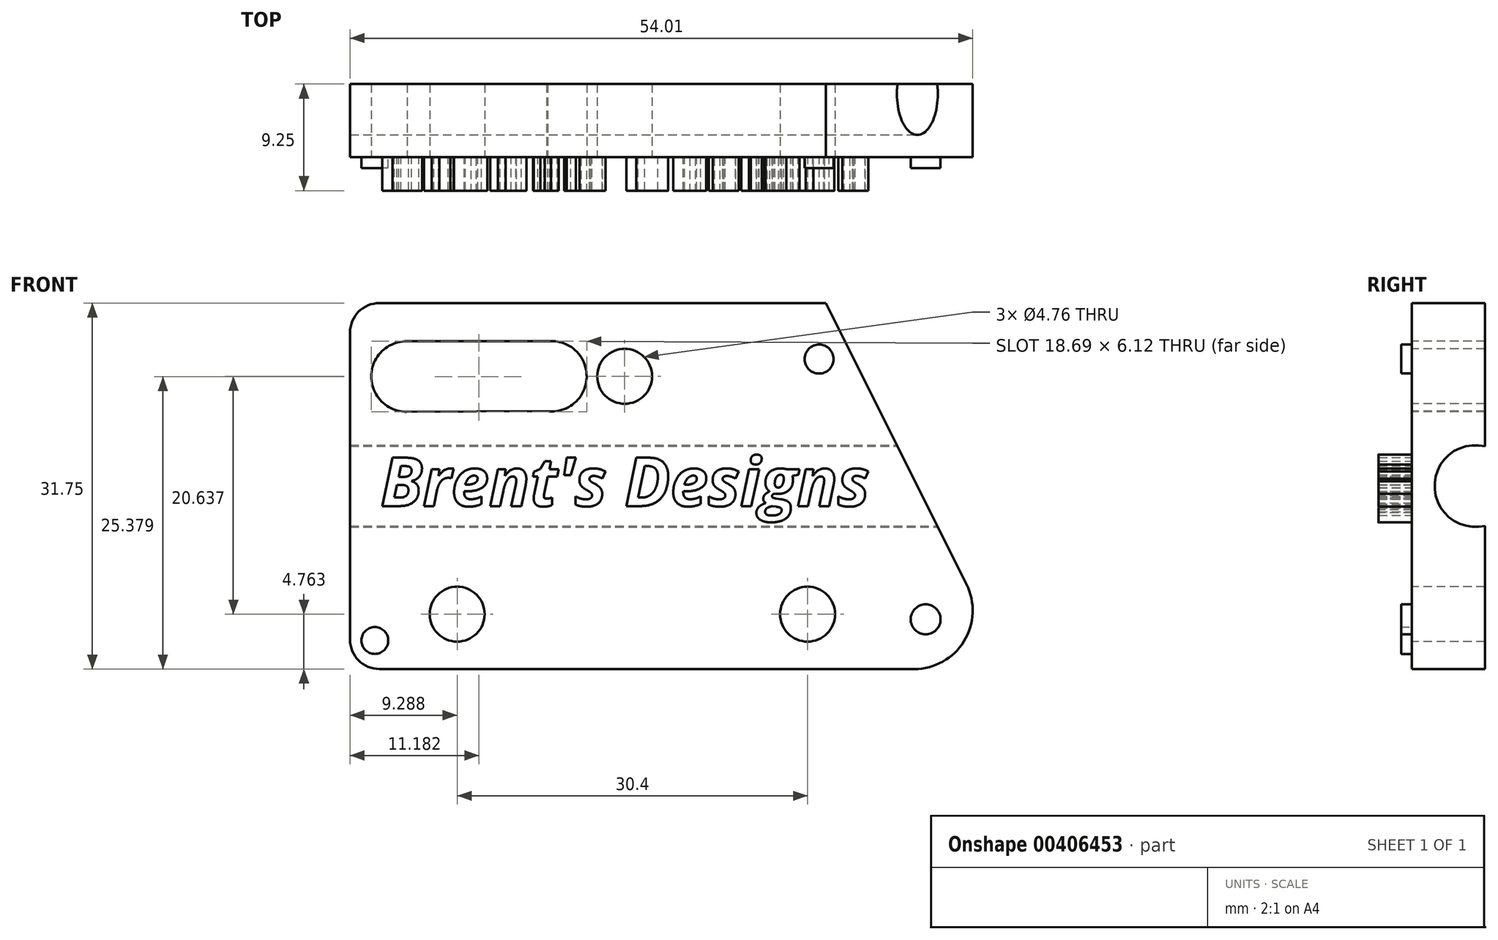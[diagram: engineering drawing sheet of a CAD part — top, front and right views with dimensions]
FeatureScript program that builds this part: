
annotation { "Feature Type Name" : "Feature", "Feature Type Description" : "" }
export const myFeature = defineFeature(function(context is Context, id is Id, definition is map)
    precondition{}
    {
        {
            var Q0;
            Q0=qCreatedBy(makeId("Right.planeOp"),FACE);
            var sketch = newSketch(context, id + "F0", { "sketchPlane" : qUnion([Q0])});
            skLineSegment(sketch, "E0.bottom", {"start": v(0, 0) * mm, "end": v(6.35, 0) * mm});
            skLineSegment(sketch, "E0.top", {"start": v(0, 31.75) * mm, "end": v(6.35, 31.75) * mm});
            skLineSegment(sketch, "E0.left", {"start": v(0, 0) * mm, "end": v(0, 31.75) * mm});
            skLineSegment(sketch, "E1", {"start": v(6.35, 31.75) * mm, "end": v(6.35, 19.33) * mm});
            skArc(sketch, "E2", {"start": v(6.35, 19.33) * mm, "mid": v(1.94, 15.88) * mm, "end": v(6.35, 12.42) * mm});
            skPoint(sketch, "E3.start.orphan", {"position": v(6.35, 15.88) * mm});
            skLineSegment(sketch, "E4.trimOffspring", {"start": v(6.35, 12.42) * mm, "end": v(6.35, 0) * mm});
            skSolve(sketch);
        }
        {
            var Q0;
            Q0=makeQuery(id+"F0.imprint","IMPRINT",FACE,{"disambiguationData":[TD([[makeQuery(id+"F0.imprint","IMPRINT",EDGE,{"derivedFrom":sQuery(id+"F0.wireOp",EDGE,"E0.bottom")}),1.0]])]});
            extrude(context, id + "F1", {"entities" : qUnion([Q0]), "oppositeDirection" : true, "depth" : 57.15 * mm});
        }
        {
            var Q0;
            Q0=makeQuery(id+"F1.opExtrude","SWEPT_FACE",FACE,{"disambiguationData":[OSD([sQuery(id+"F0.wireOp",EDGE,"E0.left")])]});
            var sketch = newSketch(context, id + "F2", { "sketchPlane" : qUnion([Q0])});
            skLineSegment(sketch, "E5", {"start": v(0, 31.75) * mm, "end": v(-15.88, 31.75) * mm});
            skLineSegment(sketch, "E6", {"start": v(-15.88, 31.75) * mm, "end": v(0, 0) * mm});
            skLineSegment(sketch, "E7", {"start": v(0, 0) * mm, "end": v(0, 31.75) * mm});
            skSolve(sketch);
        }
        {
            var Q0;
            Q0=makeQuery(id+"F2.imprint","IMPRINT",FACE,{"disambiguationData":[TD([[makeQuery(id+"F2.imprint","IMPRINT",EDGE,{"derivedFrom":sQuery(id+"F2.wireOp",EDGE,"E5")}),-1.0]])]});
            extrude(context, id + "F3", {"entities" : qUnion([Q0]), "operationType" : NewBodyOperationType.REMOVE, "oppositeDirection" : true, "depth" : 10.92 * mm});
        }
        {
            var Q0;
            Q0=makeQuery(id+"F1.opExtrude","SWEPT_FACE",FACE,{"disambiguationData":[OSD([sQuery(id+"F0.wireOp",EDGE,"E0.left")])]});
            var sketch = newSketch(context, id + "F4", { "sketchPlane" : qUnion([Q0])});
            skSolve(sketch);
        }
        {
            var Q0;
            {var subQ0=sQuery(id+"F0.wireOp",EDGE,"E0.bottom");Q0=makeQuery(id+"F3.boolean.opBoolean","MERGE",EDGE,{"derivedFrom":[makeQuery(id+"F1.opExtrude","CAP_EDGE",EDGE,{"disambiguationData":[OSD([subQ0])],"isStart":true}),makeQuery(id+"F3.opExtrude","SWEPT_EDGE",EDGE,{"disambiguationData":[OSD([subQ0,sQuery(id+"F0.wireOp",EDGE,"E0.left"),sQuery(id+"F2.wireOp",EDGE,"E6"),sQuery(id+"F2.wireOp",EDGE,"E7")])]})]});}
            fillet(context, id + "F5", {"entities" : qUnion([Q0]), "radius" : 5.08 * mm, "tangentPropagation" : true, "allowEdgeOverflow" : false});
        }
        {
            var Q0;
            Q0=makeQuery(id+"F1.opExtrude","CAP_EDGE",EDGE,{"disambiguationData":[OSD([sQuery(id+"F0.wireOp",EDGE,"E0.top")])],"isStart":false});
            var Q1;
            Q1=makeQuery(id+"F1.opExtrude","CAP_EDGE",EDGE,{"disambiguationData":[OSD([sQuery(id+"F0.wireOp",EDGE,"E0.bottom")])],"isStart":false});
            var Q2;
            Q2=makeQuery(id+"F3.boolean.opBoolean","COPY",EDGE,{"derivedFrom":makeQuery(id+"F3.opExtrude","SWEPT_EDGE",EDGE,{"disambiguationData":[OSD([sQuery(id+"F0.wireOp",EDGE,"E0.top"),sQuery(id+"F0.wireOp",EDGE,"E0.left"),sQuery(id+"F2.wireOp",EDGE,"E5"),sQuery(id+"F2.wireOp",EDGE,"E6")])]})});
            fillet(context, id + "F6", {"entities" : qUnion([Q0, Q1, Q2]), "radius" : 2.54 * mm, "tangentPropagation" : true, "allowEdgeOverflow" : false});
        }
        {
            var Q0;
            {var subQ0=sQuery(id+"F0.wireOp",EDGE,"E0.left");Q0=makeQuery(id+"F4.imprint","IMPRINT",FACE,{"disambiguationData":[TD([[makeQuery(id+"F4.imprint","IMPRINT",EDGE,{"derivedFrom":makeQuery(id+"F1.opExtrude","CAP_EDGE",EDGE,{"disambiguationData":[OSD([subQ0])],"isStart":false})}),-1.0]])]});}
            var sketch = newSketch(context, id + "F7", { "sketchPlane" : qUnion([Q0])});
            skCircle(sketch, "E8", {"center": v(-17.46, 4.76) * mm, "radius": 2.38 * mm});
            skCircle(sketch, "E9", {"center": v(-47.86, 4.76) * mm, "radius": 2.38 * mm});
            skCircle(sketch, "E10", {"center": v(-33.33, 25.4) * mm, "radius": 2.38 * mm});
            skPoint(sketch, "E11.center.orphan", {"position": v(-39.68, 25.4) * mm});
            skArc(sketch, "E12", {"start": v(-40.12, 22.37) * mm, "mid": v(-36.62, 25.34) * mm, "end": v(-40, 28.44) * mm});
            skArc(sketch, "E13", {"start": v(-52.2, 28.44) * mm, "mid": v(-55.31, 25.4) * mm, "end": v(-52.23, 22.32) * mm});
            skLineSegment(sketch, "E14", {"start": v(-52.3, 28.44) * mm, "end": v(-39.35, 28.44) * mm});
            skLineSegment(sketch, "E15", {"start": v(-52.23, 22.32) * mm, "end": v(-39.21, 22.38) * mm});
            skSolve(sketch);
        }
        {
            var Q0;
            {var subQ0=sQuery(id+"F0.wireOp",EDGE,"E0.left");Q0=makeQuery(id+"F4.imprint","IMPRINT",FACE,{"disambiguationData":[TD([[makeQuery(id+"F4.imprint","IMPRINT",EDGE,{"derivedFrom":makeQuery(id+"F1.opExtrude","CAP_EDGE",EDGE,{"disambiguationData":[OSD([subQ0])],"isStart":false})}),-1.0]])]});}
            var sketch = newSketch(context, id + "F8", { "sketchPlane" : qUnion([Q0])});
            skSolve(sketch);
        }
        {
            var Q0;
            Q0 = qSketchRegion(id + "F7", true);
            extrude(context, id + "F9", {"entities" : qUnion([Q0]), "operationType" : NewBodyOperationType.REMOVE, "oppositeDirection" : true, "depth" : 25.4 * mm});
        }
        {
            var Q0;
            {var subQ0=sQuery(id+"F0.wireOp",EDGE,"E0.left");Q0=makeQuery(id+"F8.imprint","IMPRINT",FACE,{"disambiguationData":[TD([[makeQuery(id+"F8.imprint","IMPRINT",EDGE,{"derivedFrom":makeQuery(id+"F4.imprint","IMPRINT",EDGE,{"derivedFrom":makeQuery(id+"F1.opExtrude","CAP_EDGE",EDGE,{"disambiguationData":[OSD([subQ0])],"isStart":false})})}),-1.0]])]});}
            var sketch = newSketch(context, id + "F10", { "sketchPlane" : qUnion([Q0])});
            skText(sketch, "E16", { "text": "Brent\'s Designs", "fontName": "OpenSans-BoldItalic.ttf"});
            const initialGuessF10  = {"E16": [-0.0545, 0.01414, 1, 0, 0.00423]};
            skSetInitialGuess(sketch, initialGuessF10);
            skSolve(sketch);
        }
        {
            var Q0;
            Q0 = qSketchRegion(id + "F10", true);
            extrude(context, id + "F11", {"entities" : qUnion([Q0]), "operationType" : NewBodyOperationType.ADD, "depth" : 2.9 * mm});
        }
        {
            var Q0;
            {var subQ0=sQuery(id+"F0.wireOp",EDGE,"E0.left");Q0=makeQuery(id+"F8.imprint","IMPRINT",FACE,{"disambiguationData":[TD([[makeQuery(id+"F8.imprint","IMPRINT",EDGE,{"derivedFrom":makeQuery(id+"F4.imprint","IMPRINT",EDGE,{"derivedFrom":makeQuery(id+"F1.opExtrude","CAP_EDGE",EDGE,{"disambiguationData":[OSD([subQ0])],"isStart":false})})}),-1.0]])]});}
            var sketch = newSketch(context, id + "F12", { "sketchPlane" : qUnion([Q0])});
            skCircle(sketch, "E17", {"center": v(-16.46, 26.9) * mm, "radius": 1.26 * mm});
            skCircle(sketch, "E18", {"center": v(-55, 2.47) * mm, "radius": 1.16 * mm});
            skCircle(sketch, "E19", {"center": v(-7.22, 4.3) * mm, "radius": 1.3 * mm});
            skSolve(sketch);
        }
        {
            var Q0;
            Q0 = qSketchRegion(id + "F12", true);
            extrude(context, id + "F13", {"entities" : qUnion([Q0]), "operationType" : NewBodyOperationType.ADD, "depth" : 0.94 * mm});
        }
    });
